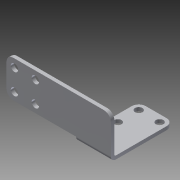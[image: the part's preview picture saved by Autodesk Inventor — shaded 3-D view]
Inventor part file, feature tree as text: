
AUTODESK INVENTOR PART (.ipt)
format: ipt  version: 2014 SP1 (Build 180222100, 222)  size: 151,040 bytes
history: native  units: in
note: dims shown in document units (in); Inventor stores cm internally (conversion verified against a paired STEP export)
features: sheet_metal_op x2, sketch x1, other x1
ambient origin geometry x8: Origin, YZ Plane, XZ Plane, XY Plane, X Axis, Y Axis, Z Axis, Center Point
bodies: Solid1 (feature_tree)
feature tree (4):
  sketch  "Sketch1"  dims[d0=0.25in d1=1.325in d2=1.25in d3=0.75in d4=0.75in d5=0.75in d6=0.75in d7=0.266in d8=0.266in d9=1.4075in d10=3.75in d11=3.5649in d12=0.2875in d13=0.2875in d14=0.25in d15=0.25in d16=0.75in d17=0.125in d18=0.125in d19=0.0625in d20=0.25in d21=0.125in d22=90.0deg d23=0.05in]
  sheet_metal_op  "Face1"
  sheet_metal_op  "Fold1"
  other  "Plate1"
